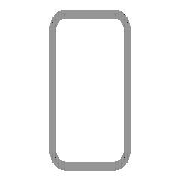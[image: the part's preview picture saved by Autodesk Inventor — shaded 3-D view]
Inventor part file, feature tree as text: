
AUTODESK INVENTOR PART (.ipt)
format: ipt  version: 2025 (Build 290162010, 162A)  size: 132,608 bytes
history: native  units: mm (DEFAULTED — no unit token found)
features: other x4, sketch x1, plane x1
ambient origin geometry x8: Origin, YZ Plane, XZ Plane, XY Plane, X Axis, Y Axis, Z Axis, Center Point
bodies: Solid1 (feature_tree), Body (feature_tree)
feature tree (6):
  parser-record x1  (decoder bookkeeping rows leaked as tree rows — omitted from the tree; the rows remain in map.json)
  other  "Driven Length"
  other  "Start Plane"
  other  "End Plane"
  sketch  "Sketch3"  dims[d3=400.0mm d4=0.0mm d7=6.0mm d9=40.0mm d11=80.0mm d12=3.0mm d13=-0.0mm d14=400.0mm d15=20.0mm d16=40.0mm d17=90.0deg d18=400.0mm]
  plane  "Work Plane3"
